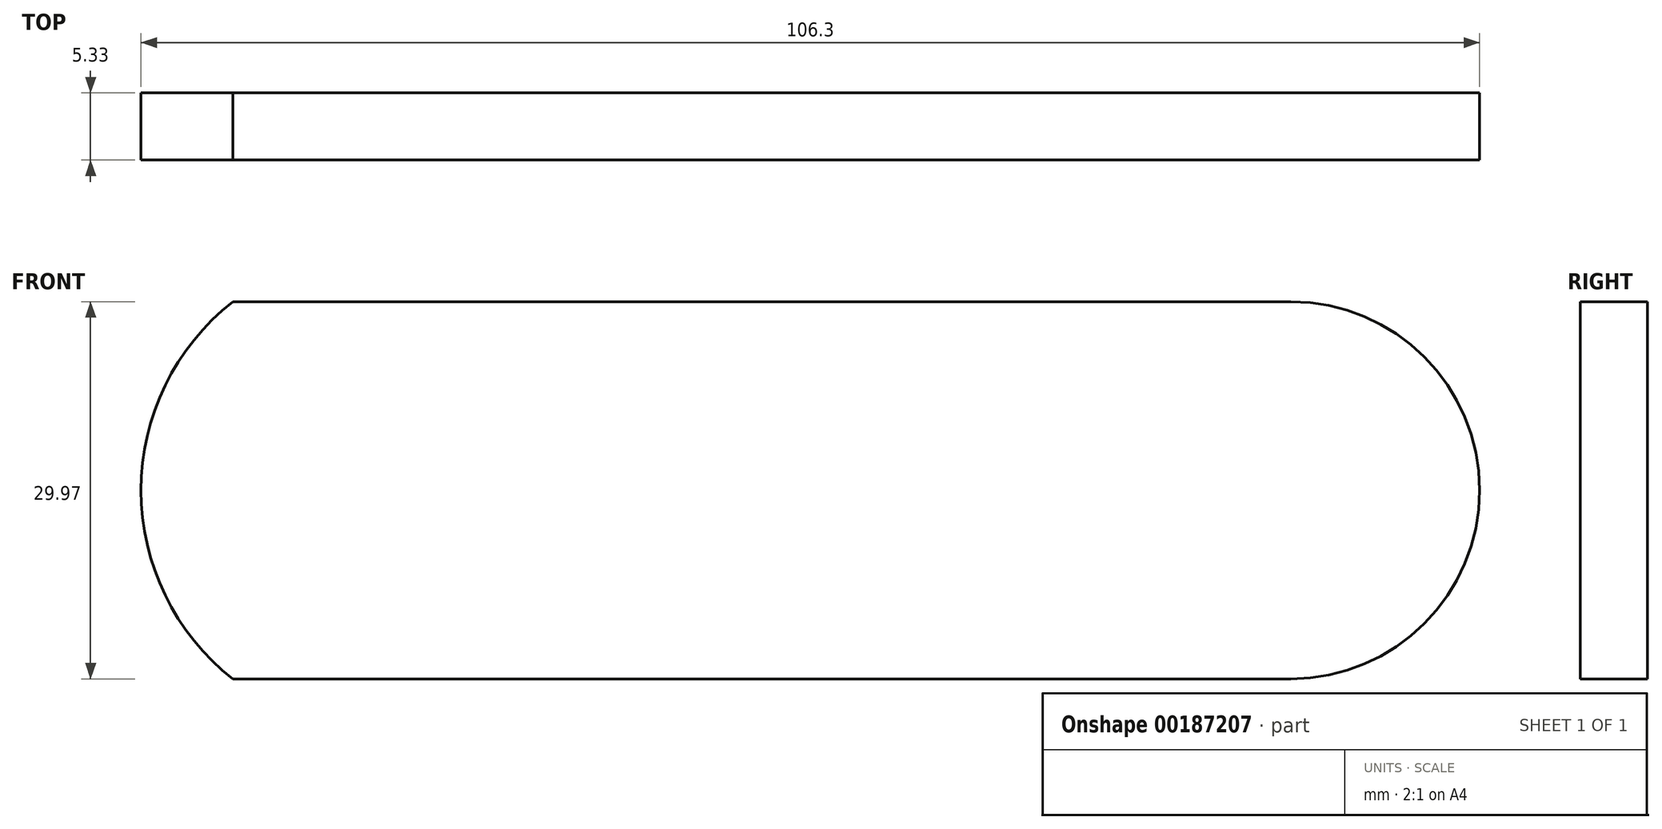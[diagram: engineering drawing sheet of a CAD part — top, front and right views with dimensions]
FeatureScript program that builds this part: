
annotation { "Feature Type Name" : "Feature", "Feature Type Description" : "" }
export const myFeature = defineFeature(function(context is Context, id is Id, definition is map)
    precondition{}
    {
        {
            var Q0;
            Q0=qCreatedBy(makeId("Front.planeOp"),FACE);
            var sketch = newSketch(context, id + "F0", { "sketchPlane" : qUnion([Q0])});
            skLineSegment(sketch, "E0.bottom", {"start": v(-40.06, 0) * mm, "end": v(43.97, 0) * mm});
            skLineSegment(sketch, "E0.top", {"start": v(-40.06, 29.97) * mm, "end": v(43.97, 29.97) * mm});
            skLineSegment(sketch, "E0.left", {"start": v(-40.06, 0) * mm, "end": v(-40.06, 29.97) * mm});
            skLineSegment(sketch, "E0.right", {"start": v(43.97, 0) * mm, "end": v(43.97, 29.97) * mm});
            skArc(sketch, "E1", {"start": v(43.97, 0) * mm, "mid": v(58.96, 14.98) * mm, "end": v(43.97, 29.97) * mm});
            skArc(sketch, "E2", {"start": v(-40.06, 29.97) * mm, "mid": v(-47.34, 14.98) * mm, "end": v(-40.06, 0) * mm});
            skSolve(sketch);
        }
        {
            var Q0;
            Q0=makeQuery(id+"F0.imprint","IMPRINT",FACE,{"disambiguationData":[TD([[makeQuery(id+"F0.imprint","IMPRINT",EDGE,{"derivedFrom":sQuery(id+"F0.wireOp",EDGE,"E0.left")}),1.0]])]});
            var Q1;
            Q1=makeQuery(id+"F0.imprint","IMPRINT",FACE,{"disambiguationData":[TD([[makeQuery(id+"F0.imprint","IMPRINT",EDGE,{"derivedFrom":sQuery(id+"F0.wireOp",EDGE,"E0.right")}),-1.0]])]});
            var Q2;
            Q2=makeQuery(id+"F0.imprint","IMPRINT",FACE,{"disambiguationData":[TD([[makeQuery(id+"F0.imprint","IMPRINT",EDGE,{"derivedFrom":sQuery(id+"F0.wireOp",EDGE,"E0.bottom")}),1.0]])]});
            extrude(context, id + "F1", {"entities" : qUnion([Q0, Q1, Q2]), "depth" : 5.33 * mm});
        }
    });
